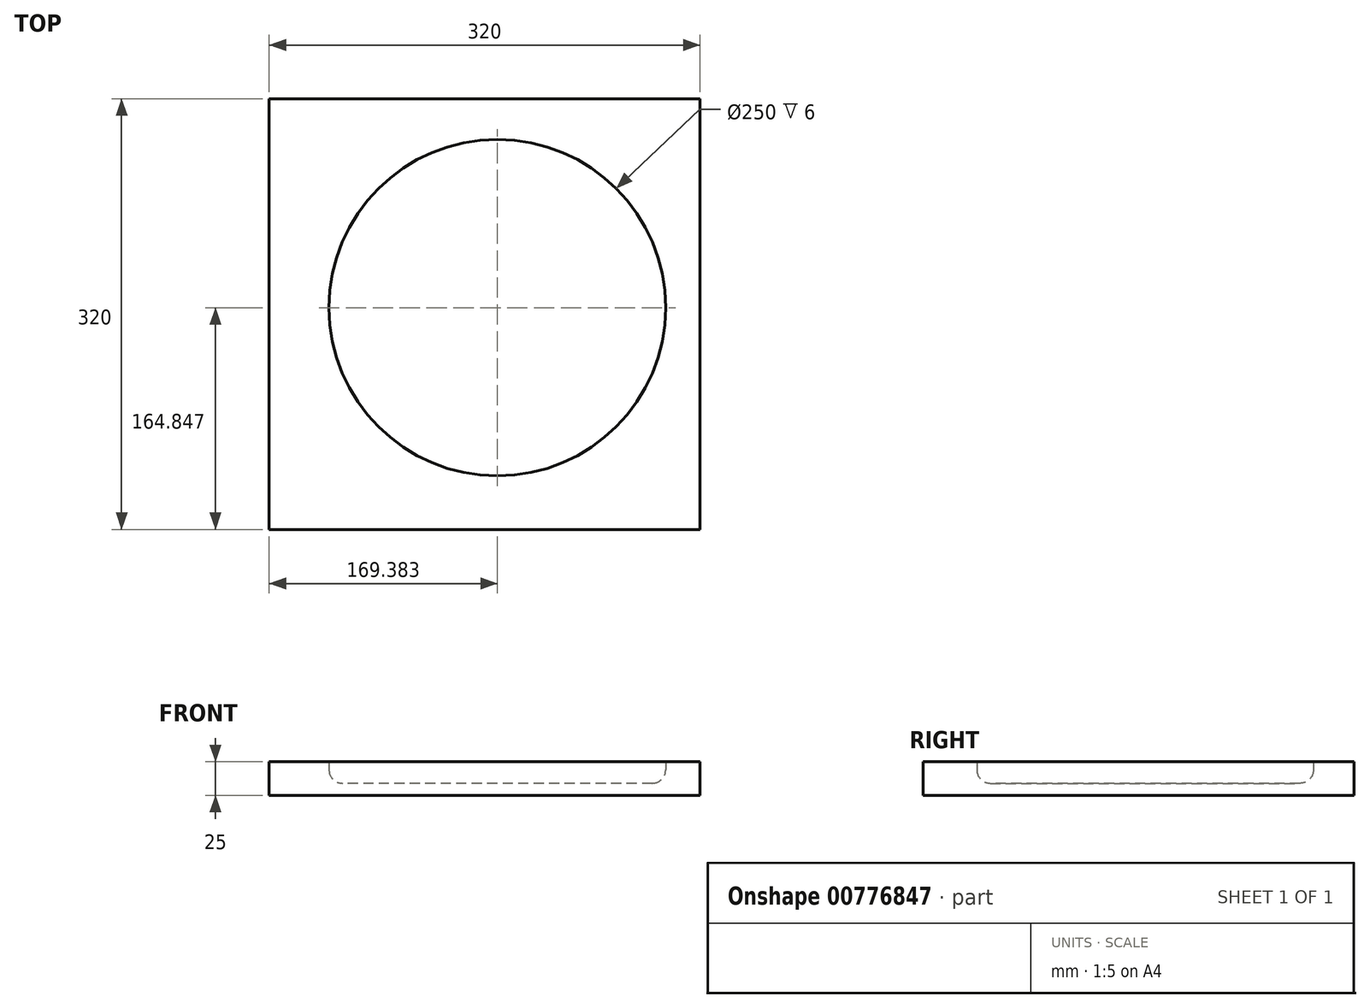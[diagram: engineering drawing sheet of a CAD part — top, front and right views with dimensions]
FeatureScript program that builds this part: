
annotation { "Feature Type Name" : "Feature", "Feature Type Description" : "" }
export const myFeature = defineFeature(function(context is Context, id is Id, definition is map)
    precondition{}
    {
        {
            var Q0;
            Q0=qCreatedBy(makeId("Top.planeOp"),FACE);
            var sketch = newSketch(context, id + "F0", { "sketchPlane" : qUnion([Q0])});
            skLineSegment(sketch, "E0.bottom", {"start": v(-153.87, 170.83) * mm, "end": v(166.13, 170.83) * mm});
            skLineSegment(sketch, "E0.top", {"start": v(-153.87, -149.17) * mm, "end": v(166.13, -149.17) * mm});
            skLineSegment(sketch, "E0.left", {"start": v(-153.87, 170.83) * mm, "end": v(-153.87, -149.17) * mm});
            skLineSegment(sketch, "E0.right", {"start": v(166.13, 170.83) * mm, "end": v(166.13, -149.17) * mm});
            skSolve(sketch);
        }
        {
            var Q0;
            Q0 = qSketchRegion(id + "F0", true);
            extrude(context, id + "F1", {"entities" : qUnion([Q0]), "depth" : 25 * mm, "offsetDistance" : 25 * mm});
        }
        {
            var Q0;
            Q0=makeQuery(id+"F1.opExtrude","CAP_FACE",FACE,{"disambiguationData":[OSD([sQuery(id+"F0.wireOp",EDGE,"E0.bottom"),sQuery(id+"F0.wireOp",EDGE,"E0.top"),sQuery(id+"F0.wireOp",EDGE,"E0.left"),sQuery(id+"F0.wireOp",EDGE,"E0.right")])],"isStart":false});
            var sketch = newSketch(context, id + "F2", { "sketchPlane" : qUnion([Q0])});
            skCircle(sketch, "E1", {"center": v(357.51, 15.68) * mm, "radius": 125 * mm});
            skSolve(sketch);
        }
        {
            var Q0;
            Q0 = qSketchRegion(id + "F2", true);
            extrude(context, id + "F3", {"entities" : qUnion([Q0]), "depth" : 20 * mm, "offsetDistance" : 25 * mm});
        }
        {
            var Q0;
            Q0=makeQuery(id+"F3.opExtrude","CAP_FACE",FACE,{"disambiguationData":[OSD([sQuery(id+"F2.wireOp",EDGE,"E1")])],"isStart":true});
            fillet(context, id + "F4", {"entities" : qUnion([Q0]), "radius" : 10 * mm, "tangentPropagation" : true, "allowEdgeOverflow" : false});
        }
        {
            var Q0;
            Q0=makeQuery(id+"F3.opExtrude","SWEPT_BODY",BODY,{"disambiguationData":[OSD([sQuery(id+"F2.wireOp",EDGE,"E1")])]});
            transform(context, id + "F5", {"entities" : qUnion([Q0]), "transformType" : TransformType.TRANSLATION_3D, "dx" : -342 * mm, "dy" : 0 * mm, "dz" : -16 * mm, "makeCopy" : false});
        }
        {
            var Q0;
            Q0=makeQuery(id+"F3.opExtrude","SWEPT_BODY",BODY,{"disambiguationData":[OSD([sQuery(id+"F2.wireOp",EDGE,"E1")])]});
            var Q1;
            Q1=makeQuery(id+"F1.opExtrude","SWEPT_BODY",BODY,{"disambiguationData":[OSD([sQuery(id+"F0.wireOp",EDGE,"E0.bottom"),sQuery(id+"F0.wireOp",EDGE,"E0.top"),sQuery(id+"F0.wireOp",EDGE,"E0.left"),sQuery(id+"F0.wireOp",EDGE,"E0.right")])]});
            booleanBodies(context, id + "F6", {"operationType" : BooleanOperationType.SUBTRACTION, "tools" : qUnion([Q0]), "targets" : qUnion([Q1])});
        }
    });
